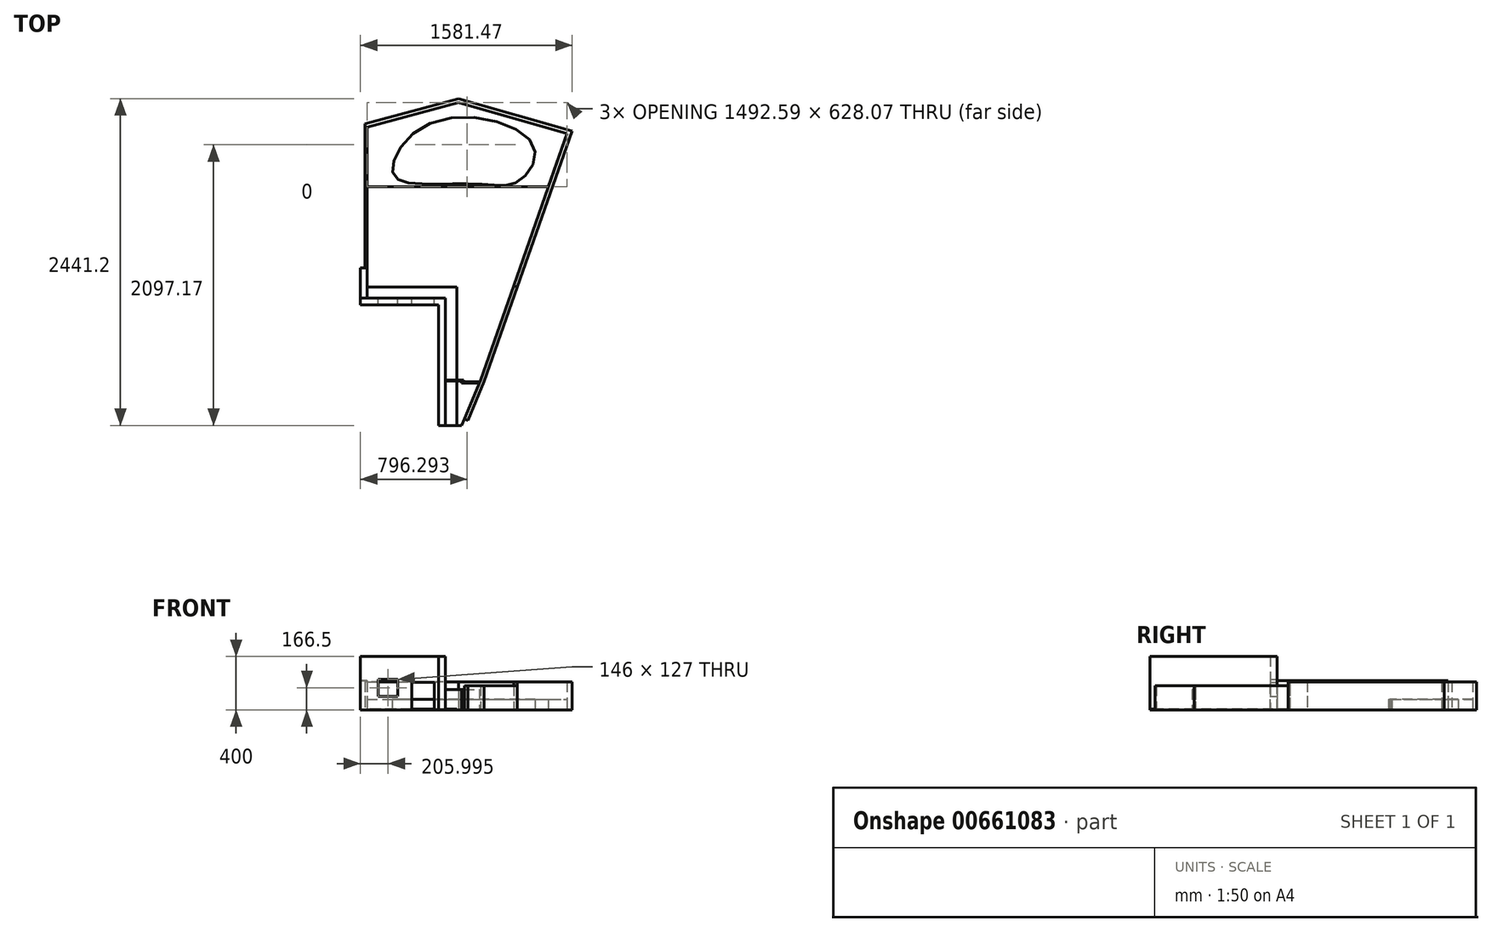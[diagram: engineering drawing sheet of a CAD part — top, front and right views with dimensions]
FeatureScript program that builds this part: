
annotation { "Feature Type Name" : "Feature", "Feature Type Description" : "" }
export const myFeature = defineFeature(function(context is Context, id is Id, definition is map)
    precondition{}
    {
        {
            var Q0;
            Q0=qCreatedBy(makeId("Top.planeOp"),FACE);
            var sketch = newSketch(context, id + "F0", { "sketchPlane" : qUnion([Q0])});
            skLineSegment(sketch, "E0", {"start": v(-157.24, -333.9) * mm, "end": v(-157.24, -196.42) * mm});
            skLineSegment(sketch, "E1", {"start": v(-157.24, -196.42) * mm, "end": v(-741.24, -196.42) * mm});
            skLineSegment(sketch, "E2", {"start": v(-741.24, -196.42) * mm, "end": v(-741.24, 636.6) * mm});
            skLineSegment(sketch, "E3", {"start": v(-741.24, 636.6) * mm, "end": v(85.76, 636.6) * mm});
            skLineSegment(sketch, "E4", {"start": v(85.76, 636.6) * mm, "end": v(85.76, 422.6) * mm});
            skLineSegment(sketch, "E5", {"start": v(85.76, 422.6) * mm, "end": v(310.76, 422.6) * mm});
            skLineSegment(sketch, "E6", {"start": v(430.76, 422.6) * mm, "end": v(536.76, 422.6) * mm});
            skLineSegment(sketch, "E7", {"start": v(-72.24, -111.42) * mm, "end": v(-72.24, -360.5) * mm});
            skLineSegment(sketch, "E8", {"start": v(-741.24, -196.42) * mm, "end": v(-791.24, -196.42) * mm});
            skLineSegment(sketch, "E9", {"start": v(-791.24, -196.42) * mm, "end": v(-791.24, 29.6) * mm});
            skLineSegment(sketch, "E10", {"start": v(-791.24, 29.6) * mm, "end": v(-737.34, 29.6) * mm});
            skPoint(sketch, "E11", {"position": v(-241.24, -196.42) * mm});
            skPoint(sketch, "E12", {"position": v(-408.24, -196.42) * mm});
            skPoint(sketch, "E13", {"position": v(-512.24, -196.42) * mm});
            skPoint(sketch, "E14", {"position": v(-658.24, -196.42) * mm});
            skPoint(sketch, "E15", {"position": v(474.79, 259.51) * mm});
            skPoint(sketch, "E16", {"position": v(342.76, -111.42) * mm});
            skLineSegment(sketch, "E17", {"start": v(310.76, 422.6) * mm, "end": v(430.76, 422.6) * mm});
            skLineSegment(sketch, "E18", {"start": v(-741.24, 636.6) * mm, "end": v(-741.24, 1082.04) * mm});
            skLineSegment(sketch, "E19", {"start": v(-741.24, 1082.04) * mm, "end": v(-59.66, 1264.67) * mm});
            skLineSegment(sketch, "E20", {"start": v(-59.66, 1264.67) * mm, "end": v(751.35, 1033.1) * mm});
            skLineSegment(sketch, "E21", {"start": v(-756.24, 29.6) * mm, "end": v(-756.24, 1082.04) * mm});
            skLineSegment(sketch, "E22", {"start": v(-741.24, 1082.04) * mm, "end": v(-756.24, 1082.04) * mm});
            skLineSegment(sketch, "E23", {"start": v(-791.24, -196.42) * mm, "end": v(-791.24, -246.42) * mm});
            skLineSegment(sketch, "E24", {"start": v(-791.24, -246.42) * mm, "end": v(-207.24, -246.42) * mm});
            skLineSegment(sketch, "E25", {"start": v(-207.24, -246.42) * mm, "end": v(-207.24, -1146.53) * mm});
            skLineSegment(sketch, "E26", {"start": v(-207.24, -1146.53) * mm, "end": v(-157.24, -1146.42) * mm});
            skLineSegment(sketch, "E27", {"start": v(-157.24, -1146.42) * mm, "end": v(-157.24, -333.9) * mm});
            skLineSegment(sketch, "E28", {"start": v(790.23, 1053.25) * mm, "end": v(-59.66, 1294.67) * mm});
            skLineSegment(sketch, "E29", {"start": v(-59.66, 1294.67) * mm, "end": v(-756.24, 1108.02) * mm});
            skLineSegment(sketch, "E30", {"start": v(-756.24, 1108.02) * mm, "end": v(-756.24, 1082.04) * mm});
            skPoint(sketch, "E31", {"position": v(-157.24, -806.42) * mm});
            skPoint(sketch, "E32", {"position": v(-157.24, -1096.42) * mm});
            skPoint(sketch, "E33", {"position": v(-15.24, -1096.42) * mm});
            skLineSegment(sketch, "E34", {"start": v(-72.24, -111.42) * mm, "end": v(-741.24, -111.42) * mm});
            skLineSegment(sketch, "E35", {"start": v(104.76, -806.42) * mm, "end": v(-15.24, -1096.42) * mm});
            skLineSegment(sketch, "E36", {"start": v(133.09, -816.3) * mm, "end": v(790.23, 1053.25) * mm});
            skLineSegment(sketch, "E37", {"start": v(104.76, -806.42) * mm, "end": v(751.35, 1033.1) * mm});
            skLineSegment(sketch, "E38", {"start": v(-157.24, -1146.42) * mm, "end": v(-72.24, -1146.42) * mm});
            skLineSegment(sketch, "E39", {"start": v(-72.24, -360.5) * mm, "end": v(-72.24, -1146.42) * mm});
            skLineSegment(sketch, "E40", {"start": v(-15.24, -1096.42) * mm, "end": v(12.48, -1107.9) * mm});
            skLineSegment(sketch, "E41", {"start": v(12.48, -1107.9) * mm, "end": v(133.09, -816.3) * mm});
            skLineSegment(sketch, "E42", {"start": v(352.41, -101.85) * mm, "end": v(380.72, -111.8) * mm});
            skLineSegment(sketch, "E43", {"start": v(-15.24, -1096.42) * mm, "end": v(-35.93, -1146.42) * mm});
            skLineSegment(sketch, "E44", {"start": v(-35.93, -1146.42) * mm, "end": v(-72.24, -1146.42) * mm});
            skLineSegment(sketch, "E45.bottom", {"start": v(-157.24, -806.42) * mm, "end": v(-35.24, -806.42) * mm});
            skLineSegment(sketch, "E45.top", {"start": v(-157.24, -814.42) * mm, "end": v(-35.24, -814.42) * mm});
            skLineSegment(sketch, "E45.left", {"start": v(-157.24, -806.42) * mm, "end": v(-157.24, -814.42) * mm});
            skLineSegment(sketch, "E46.top", {"start": v(-35.24, -821.42) * mm, "end": v(-20.24, -821.42) * mm});
            skLineSegment(sketch, "E46.left", {"start": v(-35.24, -806.42) * mm, "end": v(-35.24, -821.42) * mm});
            skLineSegment(sketch, "E46.right", {"start": v(-20.24, -806.42) * mm, "end": v(-20.24, -821.42) * mm});
            skLineSegment(sketch, "E47.bottom", {"start": v(-35.24, -821.42) * mm, "end": v(95.24, -821.42) * mm});
            skLineSegment(sketch, "E47.top", {"start": v(-35.24, -829.42) * mm, "end": v(95.24, -829.42) * mm});
            skLineSegment(sketch, "E47.left", {"start": v(-35.24, -821.42) * mm, "end": v(-35.24, -829.42) * mm});
            skLineSegment(sketch, "E47.right", {"start": v(95.24, -821.42) * mm, "end": v(95.24, -829.42) * mm});
            skFitSpline(sketch, "E48", {"points": [v(-333.53, 657.6) * mm, v(-548.85, 739.17) * mm, v(-246.3, 1120.8) * mm, v(499.8, 946.11) * mm, v(381.98, 673.89) * mm, v(130.33, 656.52) * mm, v(-333.53, 657.6) * mm]});
            skLineSegment(sketch, "E49", {"start": v(85.76, 636.6) * mm, "end": v(611.98, 636.6) * mm});
            skLineSegment(sketch, "E50", {"start": v(-35.24, -806.42) * mm, "end": v(-20.24, -806.42) * mm});
            skLineSegment(sketch, "E51", {"start": v(-741.24, 636.6) * mm, "end": v(-741.24, 240.6) * mm, "construction": true});
            skSolve(sketch);
        }
        {
            var Q0;
            Q0=makeQuery(id+"F0.imprint","IMPRINT",FACE,{"disambiguationData":[TD([[makeQuery(id+"F0.imprint","IMPRINT",EDGE,{"derivedFrom":sQuery(id+"F0.wireOp",EDGE,"E3")}),1.0]])]});
            extrude(context, id + "F1", {"entities" : qUnion([Q0]), "depth" : 78 * mm, "offsetDistance" : 25 * mm});
        }
        {
            var Q0;
            {var subQ9=sQuery(id+"F0.wireOp",EDGE,"E0");Q0=makeQuery(id+"F0.imprint","IMPRINT",FACE,{"disambiguationData":[TD([[makeQuery(id+"F0.imprint","IMPRINT",EDGE,{"derivedFrom":subQ9}),-1.0]])]});}
            var Q1;
            {var subQ0=sQuery(id+"F0.wireOp",EDGE,"E38");Q1=makeQuery(id+"F0.imprint","IMPRINT",FACE,{"disambiguationData":[TD([[makeQuery(id+"F0.imprint","IMPRINT",EDGE,{"derivedFrom":subQ0}),1.0]])]});}
            extrude(context, id + "F2", {"entities" : qUnion([Q0, Q1]), "depth" : 5 * mm, "offsetDistance" : 25 * mm});
        }
        {
            var Q0;
            {var subQ1=sQuery(id+"F0.wireOp",EDGE,"E8");Q0=makeQuery(id+"F0.imprint","IMPRINT",FACE,{"disambiguationData":[TD([[makeQuery(id+"F0.imprint","IMPRINT",EDGE,{"derivedFrom":subQ1}),-1.0]])]});}
            extrude(context, id + "F3", {"entities" : qUnion([Q0]), "operationType" : NewBodyOperationType.ADD, "depth" : 220 * mm, "offsetDistance" : 25 * mm});
        }
        {
            var Q0;
            {var subQ0=sQuery(id+"F0.wireOp",EDGE,"E18");Q0=makeQuery(id+"F0.imprint","IMPRINT",FACE,{"disambiguationData":[TD([[makeQuery(id+"F0.imprint","IMPRINT",EDGE,{"derivedFrom":subQ0}),1.0]])]});}
            extrude(context, id + "F4", {"entities" : qUnion([Q0]), "depth" : 220 * mm, "offsetDistance" : 25 * mm});
        }
        {
            var Q0;
            {var subQ1=sQuery(id+"F0.wireOp",EDGE,"E0");Q0=makeQuery(id+"F0.imprint","IMPRINT",FACE,{"disambiguationData":[TD([[makeQuery(id+"F0.imprint","IMPRINT",EDGE,{"derivedFrom":subQ1}),1.0]])]});}
            extrude(context, id + "F5", {"entities" : qUnion([Q0]), "operationType" : NewBodyOperationType.ADD, "depth" : 400 * mm, "offsetDistance" : 25 * mm});
        }
        {
            var Q0;
            Q0=makeQuery(id+"F5.opExtrude","SWEPT_FACE",FACE,{"disambiguationData":[OSD([sQuery(id+"F0.wireOp",EDGE,"E1"),sQuery(id+"F0.wireOp",EDGE,"E8")])]});
            var sketch = newSketch(context, id + "F6", { "sketchPlane" : qUnion([Q0])});
            skLineSegment(sketch, "E52", {"start": v(241.24, 5) * mm, "end": v(241.24, 205) * mm});
            skLineSegment(sketch, "E53", {"start": v(241.24, 205) * mm, "end": v(408.24, 205) * mm});
            skLineSegment(sketch, "E54", {"start": v(408.24, 205) * mm, "end": v(408.24, 5) * mm});
            skLineSegment(sketch, "E55.bottom", {"start": v(512.24, 230) * mm, "end": v(658.24, 230) * mm});
            skLineSegment(sketch, "E55.top", {"start": v(512.24, 103) * mm, "end": v(658.24, 103) * mm});
            skLineSegment(sketch, "E55.left", {"start": v(512.24, 230) * mm, "end": v(512.24, 103) * mm});
            skLineSegment(sketch, "E55.right", {"start": v(658.24, 230) * mm, "end": v(658.24, 103) * mm});
            skSolve(sketch);
        }
        {
            var Q0;
            {var subQ0=sQuery(id+"F6.wireOp",EDGE,"E52");Q0=makeQuery(id+"F6.imprint","IMPRINT",FACE,{"disambiguationData":[TD([[makeQuery(id+"F6.imprint","IMPRINT",EDGE,{"derivedFrom":subQ0}),-1.0]])]});}
            var Q1;
            Q1=makeQuery(id+"F6.imprint","IMPRINT",FACE,{"disambiguationData":[TD([[makeQuery(id+"F6.imprint","IMPRINT",EDGE,{"derivedFrom":sQuery(id+"F6.wireOp",EDGE,"E55.bottom")}),-1.0]])]});
            extrude(context, id + "F7", {"entities" : qUnion([Q0, Q1]), "operationType" : NewBodyOperationType.REMOVE, "oppositeDirection" : true, "depth" : 200 * mm, "offsetDistance" : 25 * mm});
        }
        {
            var Q0;
            Q0=makeQuery(id+"F0.imprint","IMPRINT",FACE,{"disambiguationData":[TD([[makeQuery(id+"F0.imprint","IMPRINT",EDGE,{"derivedFrom":sQuery(id+"F0.wireOp",EDGE,"E19")}),1.0]])]});
            extrude(context, id + "F8", {"entities" : qUnion([Q0]), "depth" : 208 * mm, "offsetDistance" : 25 * mm});
        }
        {
            var Q0;
            {var subQ7=sQuery(id+"F0.wireOp",EDGE,"E40");Q0=makeQuery(id+"F0.imprint","IMPRINT",FACE,{"disambiguationData":[TD([[makeQuery(id+"F0.imprint","IMPRINT",EDGE,{"derivedFrom":subQ7}),1.0]])]});}
            extrude(context, id + "F9", {"entities" : qUnion([Q0]), "depth" : 180 * mm, "offsetDistance" : 25 * mm});
        }
        {
            var Q0;
            {var subQ0=sQuery(id+"F0.wireOp",EDGE,"E45.bottom");var subQ1=sQuery(id+"F0.wireOp",EDGE,"E27");var subQ2=makeQuery(id+"F0.imprint","INTERSECT",VERTEX,{"derivedFrom":[subQ1,subQ0]});Q0=makeQuery(id+"F0.imprint","IMPRINT",FACE,{"disambiguationData":[TD([[makeQuery(id+"F0.imprint","IMPRINT",EDGE,{"disambiguationData":[TD([[subQ2,1.0]])],"derivedFrom":subQ1}),-1.0]])]});}
            var Q1;
            {var subQ0=sQuery(id+"F0.wireOp",EDGE,"E45.top");var subQ1=sQuery(id+"F0.wireOp",EDGE,"E39");var subQ2=makeQuery(id+"F0.imprint","INTERSECT",VERTEX,{"derivedFrom":[subQ1,subQ0]});Q1=makeQuery(id+"F0.imprint","IMPRINT",FACE,{"disambiguationData":[TD([[makeQuery(id+"F0.imprint","IMPRINT",EDGE,{"disambiguationData":[TD([[subQ2,1.0]])],"derivedFrom":subQ1}),1.0]])]});}
            var Q2;
            {var subQ5=sQuery(id+"F0.wireOp",EDGE,"E46.bottom");Q2=makeQuery(id+"F0.imprint","IMPRINT",FACE,{"disambiguationData":[TD([[makeQuery(id+"F0.imprint","IMPRINT",EDGE,{"derivedFrom":subQ5}),-1.0]])]});}
            var Q3;
            Q3=makeQuery(id+"F0.imprint","IMPRINT",FACE,{"disambiguationData":[TD([[makeQuery(id+"F0.imprint","IMPRINT",EDGE,{"derivedFrom":sQuery(id+"F0.wireOp",EDGE,"E46.top")}),-1.0]])]});
            var Q4;
            {var subQ2=sQuery(id+"F0.wireOp",EDGE,"E46.top");Q4=makeQuery(id+"F0.imprint","IMPRINT",FACE,{"disambiguationData":[TD([[makeQuery(id+"F0.imprint","IMPRINT",EDGE,{"derivedFrom":subQ2}),1.0]])]});}
            extrude(context, id + "F10", {"entities" : qUnion([Q0, Q1, Q2, Q3, Q4]), "depth" : 152 * mm, "offsetDistance" : 25 * mm});
        }
        {
            var Q0;
            Q0=makeQuery(id+"F0.imprint","IMPRINT",FACE,{"disambiguationData":[TD([[makeQuery(id+"F0.imprint","IMPRINT",EDGE,{"derivedFrom":sQuery(id+"F0.wireOp",EDGE,"E48")}),-1.0]])]});
            extrude(context, id + "F11", {"entities" : qUnion([Q0]), "depth" : 79 * mm, "offsetDistance" : 25 * mm});
        }
        {
            var Q0;
            {var subQ9=sQuery(id+"F0.wireOp",EDGE,"E3");Q0=makeQuery(id+"F0.imprint","IMPRINT",FACE,{"disambiguationData":[TD([[makeQuery(id+"F0.imprint","IMPRINT",EDGE,{"derivedFrom":subQ9}),-1.0]])]});}
            var Q1;
            Q1=makeQuery(id+"F0.imprint","IMPRINT",FACE,{"disambiguationData":[TD([[makeQuery(id+"F0.imprint","IMPRINT",EDGE,{"derivedFrom":sQuery(id+"F0.wireOp",EDGE,"E4")}),1.0]])]});
            extrude(context, id + "F12", {"entities" : qUnion([Q0, Q1]), "depth" : 1 * mm, "offsetDistance" : 25 * mm});
        }
        {
            var Q0;
            {var subQ2=sQuery(id+"F0.wireOp",EDGE,"E43");Q0=makeQuery(id+"F0.imprint","IMPRINT",FACE,{"disambiguationData":[TD([[makeQuery(id+"F0.imprint","IMPRINT",EDGE,{"derivedFrom":subQ2}),-1.0]])]});}
            extrude(context, id + "F13", {"entities" : qUnion([Q0]), "depth" : 1 * mm, "offsetDistance" : 25 * mm});
        }
    });
